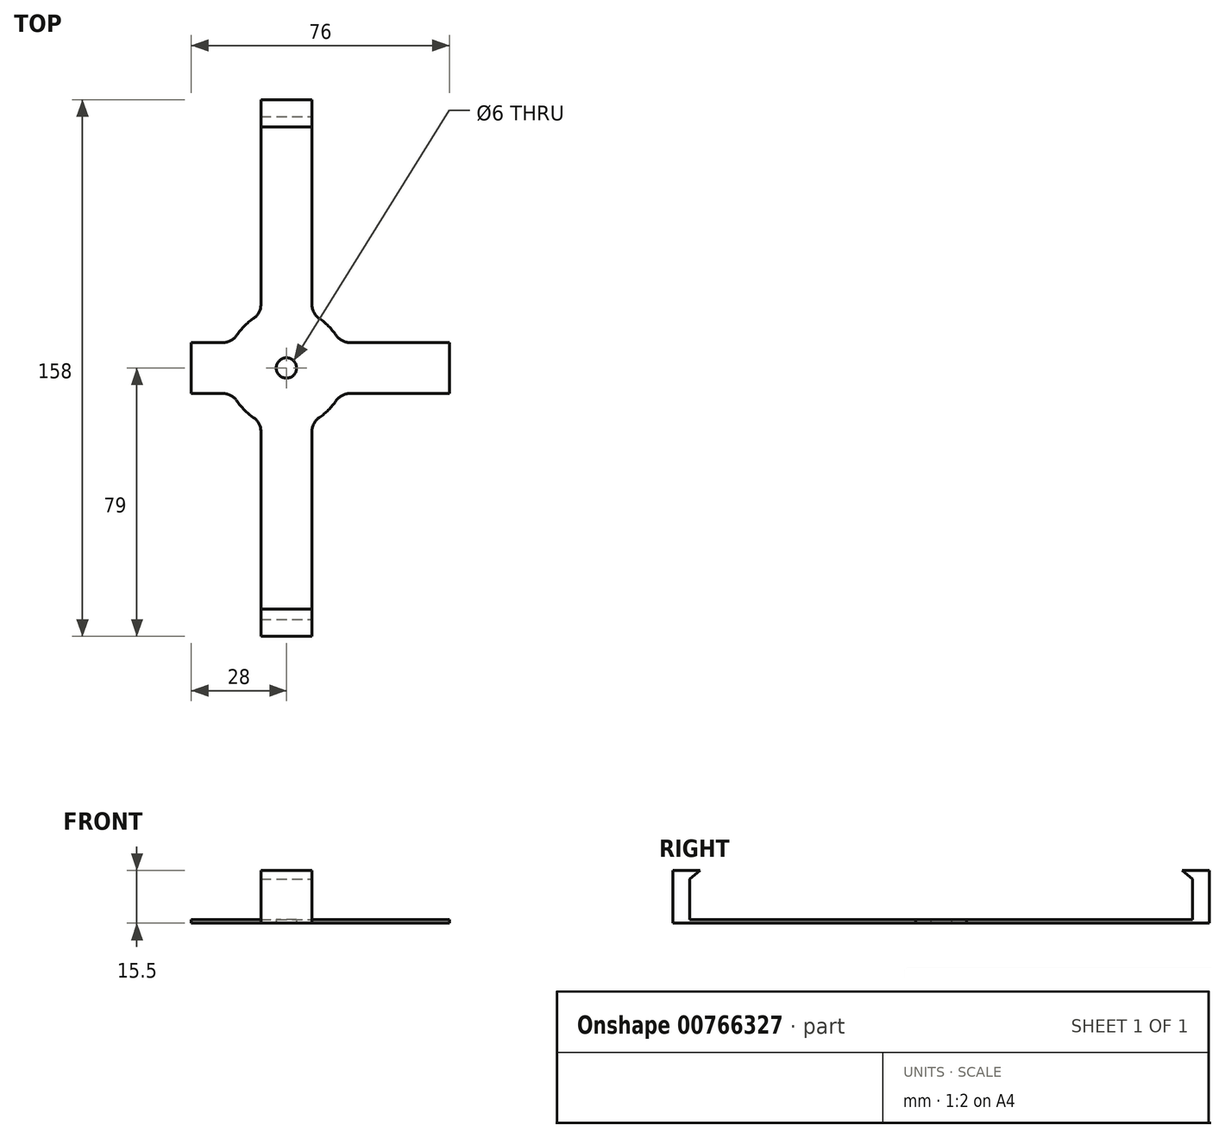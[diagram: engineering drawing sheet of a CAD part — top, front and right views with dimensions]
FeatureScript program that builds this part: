
annotation { "Feature Type Name" : "Feature", "Feature Type Description" : "" }
export const myFeature = defineFeature(function(context is Context, id is Id, definition is map)
    precondition{}
    {
        {
            var Q0;
            Q0=qCreatedBy(makeId("Top.planeOp"),FACE);
            var sketch = newSketch(context, id + "F0", { "sketchPlane" : qUnion([Q0])});
            skArc(sketch, "E0", {"start": v(-9.72, 14.55) * mm, "mid": v(-12.37, 12.37) * mm, "end": v(-14.55, 9.72) * mm});
            skLineSegment(sketch, "E1", {"start": v(-7.5, 18.7) * mm, "end": v(-7.5, 74) * mm});
            skLineSegment(sketch, "E2", {"start": v(-7.5, 74) * mm, "end": v(7.5, 74) * mm});
            skLineSegment(sketch, "E3", {"start": v(7.5, 74) * mm, "end": v(7.5, 18.7) * mm});
            skPoint(sketch, "E4.visualSharp", {"position": v(-7.5, 15.81) * mm});
            skArc(sketch, "E4.filletArc", {"start": v(-9.72, 14.55) * mm, "mid": v(-8.1, 16.35) * mm, "end": v(-7.5, 18.7) * mm});
            skPoint(sketch, "E5.visualSharp", {"position": v(7.5, 15.81) * mm});
            skArc(sketch, "E5.filletArc", {"start": v(7.5, 18.7) * mm, "mid": v(8.1, 16.35) * mm, "end": v(9.72, 14.55) * mm});
            skPoint(sketch, "E6.endSnap0", {"position": v(0, -17.5) * mm});
            skLineSegment(sketch, "E7", {"start": v(-7.5, -18.7) * mm, "end": v(-7.5, -74) * mm});
            skLineSegment(sketch, "E8", {"start": v(-7.5, -74) * mm, "end": v(7.5, -74) * mm});
            skLineSegment(sketch, "E9", {"start": v(7.5, -74) * mm, "end": v(7.5, -18.7) * mm});
            skArc(sketch, "E10.trimOffspring", {"start": v(9.72, -14.55) * mm, "mid": v(12.37, -12.37) * mm, "end": v(14.55, -9.72) * mm});
            skPoint(sketch, "E11.orphan", {"position": v(7.5, 0) * mm});
            skPoint(sketch, "E12.visualSharp", {"position": v(-7.5, -15.81) * mm});
            skArc(sketch, "E12.filletArc", {"start": v(-7.5, -18.7) * mm, "mid": v(-8.1, -16.35) * mm, "end": v(-9.72, -14.55) * mm});
            skPoint(sketch, "E13.visualSharp", {"position": v(7.5, -15.81) * mm});
            skArc(sketch, "E13.filletArc", {"start": v(9.72, -14.55) * mm, "mid": v(8.1, -16.35) * mm, "end": v(7.5, -18.7) * mm});
            skCircle(sketch, "E14", {"center": v(0, 0) * mm, "radius": 3 * mm});
            skLineSegment(sketch, "E15", {"start": v(0, 0) * mm, "end": v(0, 7.5) * mm});
            skLineSegment(sketch, "E16", {"start": v(-18.7, 7.5) * mm, "end": v(-28, 7.5) * mm});
            skLineSegment(sketch, "E17", {"start": v(-28, 7.5) * mm, "end": v(-28, -7.5) * mm});
            skLineSegment(sketch, "E18", {"start": v(-28, -7.5) * mm, "end": v(-18.7, -7.5) * mm});
            skArc(sketch, "E19.trimOffspring", {"start": v(-14.55, -9.72) * mm, "mid": v(-12.37, -12.37) * mm, "end": v(-9.72, -14.55) * mm});
            skPoint(sketch, "E20.visualSharp", {"position": v(-15.81, 7.5) * mm});
            skArc(sketch, "E20.filletArc", {"start": v(-18.7, 7.5) * mm, "mid": v(-16.35, 8.1) * mm, "end": v(-14.55, 9.72) * mm});
            skPoint(sketch, "E21.visualSharp", {"position": v(-15.81, -7.5) * mm});
            skArc(sketch, "E21.filletArc", {"start": v(-14.55, -9.72) * mm, "mid": v(-16.35, -8.1) * mm, "end": v(-18.7, -7.5) * mm});
            skLineSegment(sketch, "E22", {"start": v(18.7, 7.5) * mm, "end": v(48, 7.5) * mm});
            skLineSegment(sketch, "E23", {"start": v(48, 7.5) * mm, "end": v(48, -7.5) * mm});
            skLineSegment(sketch, "E24", {"start": v(48, -7.5) * mm, "end": v(18.7, -7.5) * mm});
            skArc(sketch, "E25.trimOffspring", {"start": v(14.55, 9.72) * mm, "mid": v(12.37, 12.37) * mm, "end": v(9.72, 14.55) * mm});
            skPoint(sketch, "E26.visualSharp", {"position": v(15.81, 7.5) * mm});
            skArc(sketch, "E26.filletArc", {"start": v(14.55, 9.72) * mm, "mid": v(16.35, 8.1) * mm, "end": v(18.7, 7.5) * mm});
            skPoint(sketch, "E27.visualSharp", {"position": v(15.81, -7.5) * mm});
            skArc(sketch, "E27.filletArc", {"start": v(18.7, -7.5) * mm, "mid": v(16.35, -8.1) * mm, "end": v(14.55, -9.72) * mm});
            skSolve(sketch);
        }
        {
            var Q0;
            Q0 = qSketchRegion(id + "F0", true);
            extrude(context, id + "F1", {"entities" : qUnion([Q0]), "depth" : 1 * mm, "offsetDistance" : 25 * mm});
        }
        {
            var Q0;
            Q0=makeQuery(id+"F1.opExtrude","SWEPT_FACE",FACE,{"disambiguationData":[OSD([sQuery(id+"F0.wireOp",EDGE,"E9")])]});
            var sketch = newSketch(context, id + "F2", { "sketchPlane" : qUnion([Q0])});
            skLineSegment(sketch, "E28.bottom", {"start": v(-74, 0) * mm, "end": v(-79, 0) * mm});
            skLineSegment(sketch, "E28.top", {"start": v(-74, 15.5) * mm, "end": v(-79, 15.5) * mm});
            skLineSegment(sketch, "E28.left", {"start": v(-74, 0) * mm, "end": v(-74, 15.5) * mm});
            skLineSegment(sketch, "E28.right", {"start": v(-79, 0) * mm, "end": v(-79, 15.5) * mm});
            skLineSegment(sketch, "E29", {"start": v(-74, 15.5) * mm, "end": v(-71, 15.5) * mm});
            skLineSegment(sketch, "E30", {"start": v(-71, 15.5) * mm, "end": v(-74, 13) * mm});
            skLineSegment(sketch, "E31.0.1", {"start": v(74, 0) * mm, "end": v(74, 1) * mm});
            skLineSegment(sketch, "E32", {"start": v(74, 0) * mm, "end": v(79, 0) * mm});
            skLineSegment(sketch, "E33", {"start": v(79, 0) * mm, "end": v(79, 15.5) * mm});
            skLineSegment(sketch, "E34", {"start": v(79, 15.5) * mm, "end": v(71, 15.5) * mm});
            skLineSegment(sketch, "E35", {"start": v(71, 15.5) * mm, "end": v(74, 13) * mm});
            skLineSegment(sketch, "E36", {"start": v(74, 13) * mm, "end": v(74, 1) * mm});
            skLineSegment(sketch, "E37.0", {"start": v(74, 1) * mm, "end": v(18.7, 1) * mm});
            skSolve(sketch);
        }
        {
            var Q0;
            Q0 = qSketchRegion(id + "F2", true);
            extrude(context, id + "F3", {"entities" : qUnion([Q0]), "operationType" : NewBodyOperationType.ADD, "oppositeDirection" : true, "depth" : 15 * mm, "offsetDistance" : 25 * mm});
        }
    });
